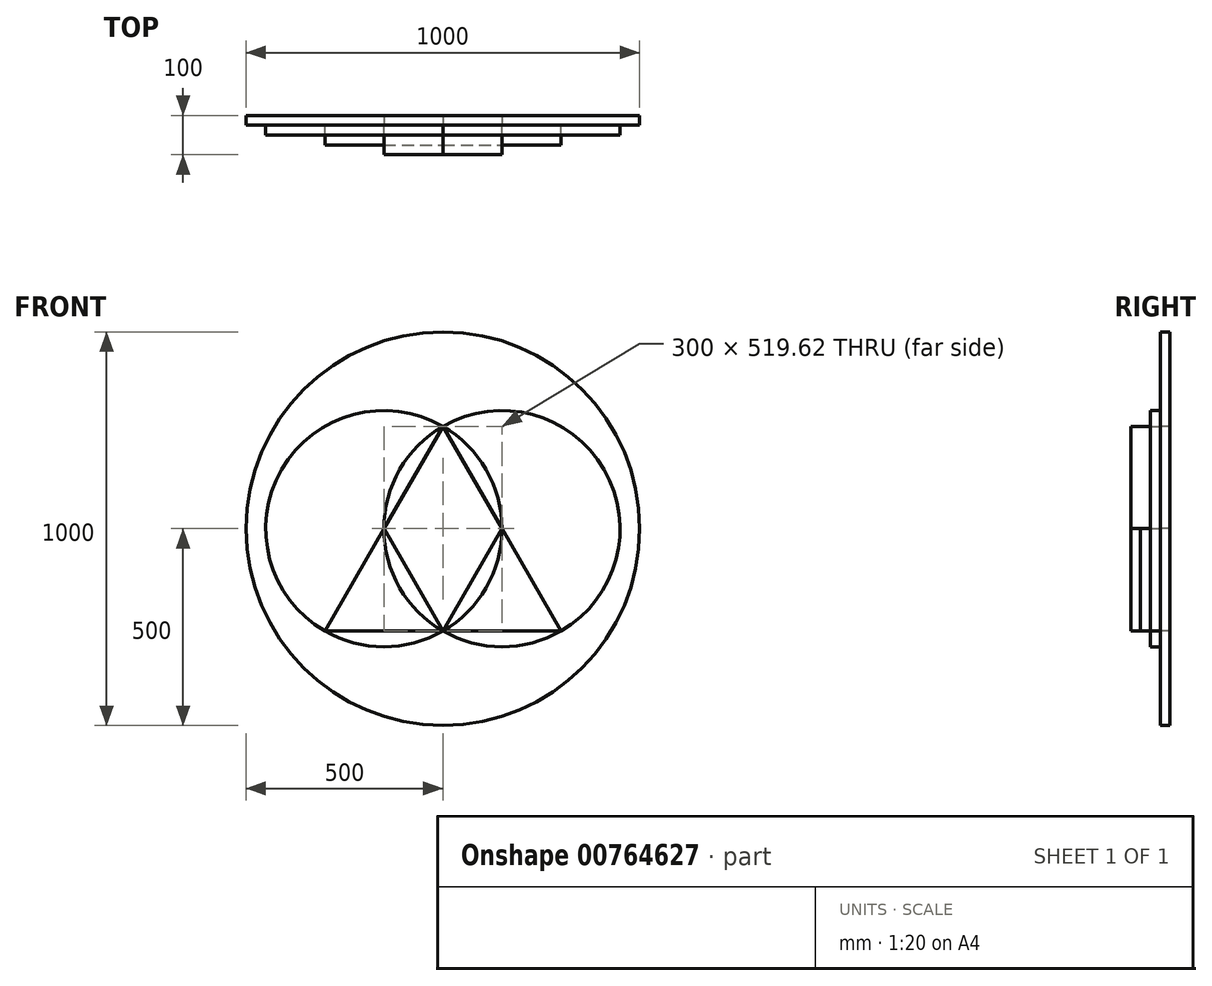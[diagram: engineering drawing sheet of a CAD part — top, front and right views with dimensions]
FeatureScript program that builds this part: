
annotation { "Feature Type Name" : "Feature", "Feature Type Description" : "" }
export const myFeature = defineFeature(function(context is Context, id is Id, definition is map)
    precondition{}
    {
        {
            var Q0;
            Q0=qCreatedBy(makeId("Front.planeOp"),FACE);
            var sketch = newSketch(context, id + "F0", { "sketchPlane" : qUnion([Q0])});
            skCircle(sketch, "E0", {"center": v(0, 0) * mm, "radius": 500 * mm});
            skSolve(sketch);
        }
        {
            var Q0;
            Q0=qCreatedBy(makeId("Front.planeOp"),FACE);
            var sketch = newSketch(context, id + "F1", { "sketchPlane" : qUnion([Q0])});
            skCircle(sketch, "E1", {"center": v(-150, 0) * mm, "radius": 300 * mm});
            skCircle(sketch, "E2", {"center": v(150, 0) * mm, "radius": 300 * mm});
            skLineSegment(sketch, "E3", {"start": v(0, -259.8) * mm, "end": v(-300, -259.8) * mm});
            skLineSegment(sketch, "E4", {"start": v(-300, -259.8) * mm, "end": v(0, 259.8) * mm});
            skLineSegment(sketch, "E5", {"start": v(0, -259.8) * mm, "end": v(300, -259.8) * mm});
            skLineSegment(sketch, "E6", {"start": v(300, -259.8) * mm, "end": v(0, 259.8) * mm});
            skLineSegment(sketch, "E7", {"start": v(0, 259.8) * mm, "end": v(0, -259.8) * mm});
            skLineSegment(sketch, "E8", {"start": v(-150, 0) * mm, "end": v(150, 0) * mm});
            skLineSegment(sketch, "E9", {"start": v(150, 0) * mm, "end": v(0, -259.8) * mm});
            skLineSegment(sketch, "E10", {"start": v(0, -259.8) * mm, "end": v(-150, 0) * mm});
            skSolve(sketch);
        }
        {
            var Q0;
            Q0=makeQuery(id+"F0.imprint","IMPRINT",FACE,{"disambiguationData":[TD([[makeQuery(id+"F0.imprint","IMPRINT",EDGE,{"derivedFrom":sQuery(id+"F0.wireOp",EDGE,"E0")}),1.0]])]});
            extrude(context, id + "F2", {"entities" : qUnion([Q0]), "oppositeDirection" : true, "depth" : 25 * mm, "offsetDistance" : 25 * mm});
        }
        {
            var Q0;
            {var subQ0=sQuery(id+"F1.wireOp",EDGE,"E4");var subQ1=sQuery(id+"F1.wireOp",EDGE,"E1");var subQ2=makeQuery(id+"F1.imprint","INTERSECT",VERTEX,{"derivedFrom":[subQ1,sQuery(id+"F1.wireOp",EDGE,"E3"),subQ0]});Q0=makeQuery(id+"F1.imprint","IMPRINT",FACE,{"disambiguationData":[TD([[makeQuery(id+"F1.imprint","IMPRINT",EDGE,{"disambiguationData":[TD([[subQ2,-1.0]])],"derivedFrom":subQ0}),1.0]])]});}
            var Q1;
            {var subQ0=sQuery(id+"F1.wireOp",EDGE,"E6");var subQ1=sQuery(id+"F1.wireOp",EDGE,"E2");var subQ5=makeQuery(id+"F1.imprint","INTERSECT",VERTEX,{"derivedFrom":[subQ1,sQuery(id+"F1.wireOp",EDGE,"E5"),subQ0]});Q1=makeQuery(id+"F1.imprint","IMPRINT",FACE,{"disambiguationData":[TD([[makeQuery(id+"F1.imprint","IMPRINT",EDGE,{"disambiguationData":[TD([[subQ5,-1.0]])],"derivedFrom":subQ0}),-1.0]])]});}
            var Q2;
            {var subQ0=sQuery(id+"F1.wireOp",EDGE,"E3");Q2=makeQuery(id+"F1.imprint","IMPRINT",FACE,{"disambiguationData":[TD([[makeQuery(id+"F1.imprint","IMPRINT",EDGE,{"derivedFrom":subQ0}),1.0]])]});}
            var Q3;
            {var subQ0=sQuery(id+"F1.wireOp",EDGE,"E5");Q3=makeQuery(id+"F1.imprint","IMPRINT",FACE,{"disambiguationData":[TD([[makeQuery(id+"F1.imprint","IMPRINT",EDGE,{"derivedFrom":subQ0}),-1.0]])]});}
            extrude(context, id + "F3", {"entities" : qUnion([Q0, Q1, Q2, Q3]), "depth" : 25 * mm, "offsetDistance" : 25 * mm});
        }
        {
            var Q0;
            {var subQ1=sQuery(id+"F1.wireOp",EDGE,"E3");Q0=makeQuery(id+"F1.imprint","IMPRINT",FACE,{"disambiguationData":[TD([[makeQuery(id+"F1.imprint","IMPRINT",EDGE,{"derivedFrom":subQ1}),-1.0]])]});}
            var Q1;
            {var subQ1=sQuery(id+"F1.wireOp",EDGE,"E5");Q1=makeQuery(id+"F1.imprint","IMPRINT",FACE,{"disambiguationData":[TD([[makeQuery(id+"F1.imprint","IMPRINT",EDGE,{"derivedFrom":subQ1}),1.0]])]});}
            extrude(context, id + "F4", {"entities" : qUnion([Q0, Q1]), "depth" : 50 * mm, "offsetDistance" : 25 * mm});
        }
        {
            var Q0;
            {var subQ0=sQuery(id+"F1.wireOp",EDGE,"E4");var subQ1=sQuery(id+"F1.wireOp",EDGE,"E2");var subQ3=makeQuery(id+"F1.imprint","INTERSECT",VERTEX,{"derivedFrom":[subQ1,subQ0,sQuery(id+"F1.wireOp",EDGE,"E8"),sQuery(id+"F1.wireOp",EDGE,"E10")]});Q0=makeQuery(id+"F1.imprint","IMPRINT",FACE,{"disambiguationData":[TD([[makeQuery(id+"F1.imprint","IMPRINT",EDGE,{"disambiguationData":[TD([[subQ3,1.0]])],"derivedFrom":subQ1}),1.0]])]});}
            var Q1;
            {var subQ0=sQuery(id+"F1.wireOp",EDGE,"E6");var subQ1=sQuery(id+"F1.wireOp",EDGE,"E1");var subQ3=makeQuery(id+"F1.imprint","INTERSECT",VERTEX,{"derivedFrom":[subQ1,subQ0,sQuery(id+"F1.wireOp",EDGE,"E8"),sQuery(id+"F1.wireOp",EDGE,"E9")]});Q1=makeQuery(id+"F1.imprint","IMPRINT",FACE,{"disambiguationData":[TD([[makeQuery(id+"F1.imprint","IMPRINT",EDGE,{"disambiguationData":[TD([[subQ3,-1.0]])],"derivedFrom":subQ1}),1.0]])]});}
            var Q2;
            {var subQ0=sQuery(id+"F1.wireOp",EDGE,"E10");Q2=makeQuery(id+"F1.imprint","IMPRINT",FACE,{"disambiguationData":[TD([[makeQuery(id+"F1.imprint","IMPRINT",EDGE,{"derivedFrom":subQ0}),1.0]])]});}
            var Q3;
            {var subQ0=sQuery(id+"F1.wireOp",EDGE,"E9");Q3=makeQuery(id+"F1.imprint","IMPRINT",FACE,{"disambiguationData":[TD([[makeQuery(id+"F1.imprint","IMPRINT",EDGE,{"derivedFrom":subQ0}),1.0]])]});}
            extrude(context, id + "F5", {"entities" : qUnion([Q0, Q1, Q2, Q3]), "depth" : 75 * mm, "offsetDistance" : 25 * mm});
        }
        {
            var Q0;
            {var subQ0=sQuery(id+"F1.wireOp",EDGE,"E7");var subQ4=sQuery(id+"F1.wireOp",EDGE,"E8");var subQ6=makeQuery(id+"F1.imprint","INTERSECT",VERTEX,{"derivedFrom":[subQ0,subQ4]});Q0=makeQuery(id+"F1.imprint","IMPRINT",FACE,{"disambiguationData":[TD([[makeQuery(id+"F1.imprint","IMPRINT",EDGE,{"disambiguationData":[TD([[subQ6,1.0]])],"derivedFrom":subQ4}),1.0]])]});}
            var Q1;
            {var subQ0=sQuery(id+"F1.wireOp",EDGE,"E7");var subQ4=sQuery(id+"F1.wireOp",EDGE,"E8");var subQ6=makeQuery(id+"F1.imprint","INTERSECT",VERTEX,{"derivedFrom":[subQ0,subQ4]});Q1=makeQuery(id+"F1.imprint","IMPRINT",FACE,{"disambiguationData":[TD([[makeQuery(id+"F1.imprint","IMPRINT",EDGE,{"disambiguationData":[TD([[subQ6,-1.0]])],"derivedFrom":subQ4}),1.0]])]});}
            var Q2;
            {var subQ0=sQuery(id+"F1.wireOp",EDGE,"E9");Q2=makeQuery(id+"F1.imprint","IMPRINT",FACE,{"disambiguationData":[TD([[makeQuery(id+"F1.imprint","IMPRINT",EDGE,{"derivedFrom":subQ0}),-1.0]])]});}
            var Q3;
            {var subQ0=sQuery(id+"F1.wireOp",EDGE,"E10");Q3=makeQuery(id+"F1.imprint","IMPRINT",FACE,{"disambiguationData":[TD([[makeQuery(id+"F1.imprint","IMPRINT",EDGE,{"derivedFrom":subQ0}),-1.0]])]});}
            extrude(context, id + "F6", {"entities" : qUnion([Q0, Q1, Q2, Q3]), "operationType" : NewBodyOperationType.REMOVE, "oppositeDirection" : true, "depth" : 300 * mm, "offsetDistance" : 25 * mm});
        }
    });
